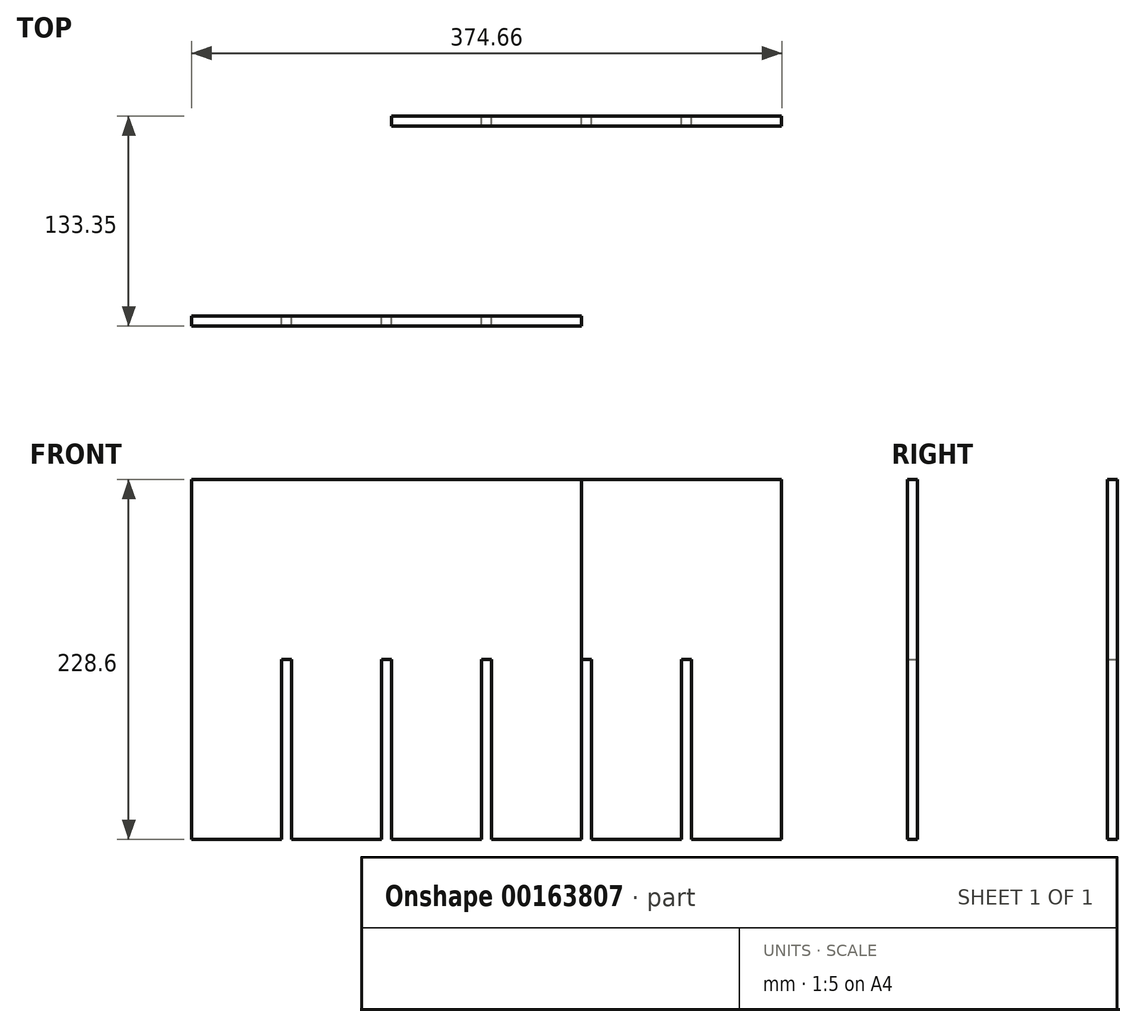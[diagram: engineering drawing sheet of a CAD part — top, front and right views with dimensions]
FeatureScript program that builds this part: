
annotation { "Feature Type Name" : "Feature", "Feature Type Description" : "" }
export const myFeature = defineFeature(function(context is Context, id is Id, definition is map)
    precondition{}
    {
        {
            var Q0;
            Q0=qCreatedBy(makeId("Front.planeOp"),FACE);
            var sketch = newSketch(context, id + "F0", { "sketchPlane" : qUnion([Q0])});
            skLineSegment(sketch, "E0.bottom", {"start": v(123.82, -114.3) * mm, "end": v(66.67, -114.3) * mm});
            skLineSegment(sketch, "E0.top", {"start": v(123.83, 114.3) * mm, "end": v(-123.83, 114.3) * mm});
            skLineSegment(sketch, "E0.left", {"start": v(123.83, -114.3) * mm, "end": v(123.83, 114.3) * mm});
            skLineSegment(sketch, "E0.right", {"start": v(-123.83, -114.3) * mm, "end": v(-123.83, 114.3) * mm});
            skPoint(sketch, "E0.middle", {"position": v(0, 0) * mm});
            skLineSegment(sketch, "E1", {"start": v(0, 114.3) * mm, "end": v(0, -114.3) * mm, "construction": true});
            skLineSegment(sketch, "E2.0", {"start": v(-3.18, 0) * mm, "end": v(-3.18, -114.3) * mm});
            skLineSegment(sketch, "E3.0", {"start": v(-66.68, 0) * mm, "end": v(-66.67, -114.3) * mm});
            skLineSegment(sketch, "E4.0", {"start": v(-60.33, 0) * mm, "end": v(-60.33, -114.3) * mm});
            skLineSegment(sketch, "E5.MirrorCS", {"start": v(3.17, 0) * mm, "end": v(3.17, -114.3) * mm});
            skLineSegment(sketch, "E6.MirrorCS", {"start": v(60.32, 0) * mm, "end": v(60.32, -114.3) * mm});
            skLineSegment(sketch, "E7.MirrorCS", {"start": v(66.67, 0) * mm, "end": v(66.67, -114.3) * mm});
            skLineSegment(sketch, "E8", {"start": v(-66.68, 0) * mm, "end": v(-60.33, 0) * mm});
            skPoint(sketch, "E9.orphan", {"position": v(-66.68, 114.3) * mm});
            skPoint(sketch, "E10.orphan", {"position": v(-60.33, 114.3) * mm});
            skPoint(sketch, "E11.orphan", {"position": v(-3.18, 114.3) * mm});
            skPoint(sketch, "E12.orphan", {"position": v(3.18, 114.3) * mm});
            skPoint(sketch, "E13.orphan", {"position": v(60.33, 114.3) * mm});
            skPoint(sketch, "E14.orphan", {"position": v(66.67, 114.3) * mm});
            skLineSegment(sketch, "E15.trimOffspring", {"start": v(60.33, 0) * mm, "end": v(66.67, 0) * mm});
            skLineSegment(sketch, "E16.trimOffspring", {"start": v(-3.18, 0) * mm, "end": v(3.17, 0) * mm});
            skLineSegment(sketch, "E17.trimOffspring", {"start": v(-66.68, -114.3) * mm, "end": v(-123.83, -114.3) * mm});
            skLineSegment(sketch, "E18.trimOffspring", {"start": v(-3.18, -114.3) * mm, "end": v(-60.32, -114.3) * mm});
            skLineSegment(sketch, "E19.trimOffspring", {"start": v(60.32, -114.3) * mm, "end": v(3.17, -114.3) * mm});
            skSolve(sketch);
        }
        {
            var Q0;
            Q0 = qSketchRegion(id + "F0", true);
            extrude(context, id + "F1", {"entities" : qUnion([Q0]), "depth" : 6.35 * mm});
        }
        {
            var Q0;
            Q0=makeQuery(id+"F1.opExtrude","SWEPT_BODY",BODY,{"disambiguationData":[OSD([sQuery(id+"F0.wireOp",EDGE,"E0.bottom"),sQuery(id+"F0.wireOp",EDGE,"E0.top"),sQuery(id+"F0.wireOp",EDGE,"E0.left"),sQuery(id+"F0.wireOp",EDGE,"E0.right"),sQuery(id+"F0.wireOp",EDGE,"E2.0"),sQuery(id+"F0.wireOp",EDGE,"E3.0"),sQuery(id+"F0.wireOp",EDGE,"E4.0"),sQuery(id+"F0.wireOp",EDGE,"E5.MirrorCS"),sQuery(id+"F0.wireOp",EDGE,"E6.MirrorCS"),sQuery(id+"F0.wireOp",EDGE,"E7.MirrorCS"),sQuery(id+"F0.wireOp",EDGE,"E8"),sQuery(id+"F0.wireOp",EDGE,"E15.trimOffspring"),sQuery(id+"F0.wireOp",EDGE,"E16.trimOffspring"),sQuery(id+"F0.wireOp",EDGE,"E17.trimOffspring"),sQuery(id+"F0.wireOp",EDGE,"E18.trimOffspring"),sQuery(id+"F0.wireOp",EDGE,"E19.trimOffspring")])]});
            transform(context, id + "F2", {"entities" : qUnion([Q0]), "transformType" : TransformType.TRANSLATION_3D, "dx" : 127 * mm, "dy" : 127 * mm, "dz" : 0 * mm, "makeCopy" : true});
        }
    });
